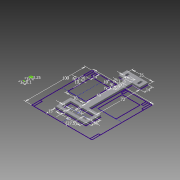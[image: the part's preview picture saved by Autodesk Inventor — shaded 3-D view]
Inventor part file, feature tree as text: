
AUTODESK INVENTOR PART (.ipt)
format: ipt  version: 2013 (Build 170138000, 138)  size: 138,240 bytes
history: native  units: mm
features: extrude x2, sketch x1
ambient origin geometry x8: Origin, YZ Plane, XZ Plane, XY Plane, X Axis, Y Axis, Z Axis, Center Point
feature tree (3):
  sketch  "Sketch1"  dims[d0=100.0mm d2=100.0mm d3=3.0mm d5=3.0mm d7=3.25mm d8=14.0mm d9=30.0mm d10=40.0mm d11=10.0mm d12=10.0mm d15=3.25mm d16=8.0mm d17=0.0mm d22=40.0mm d23=15.0mm d24=5.0mm d25=5.0mm d26=5.0mm d27=5.0mm d28=15.0mm d29=72.0mm d30=14.0mm d31=10.0mm d32=35.0mm d33=3.25mm d34=0.0mm d35=27.5mm d36=3.25mm d37=7.0mm d38=7.0mm d39=5.0mm d40=3.25mm d41=0.0mm]
  extrude  "Extrusion4"  Depth=100.0mm
  extrude  "Extrusion5"  Depth=3.0mm
